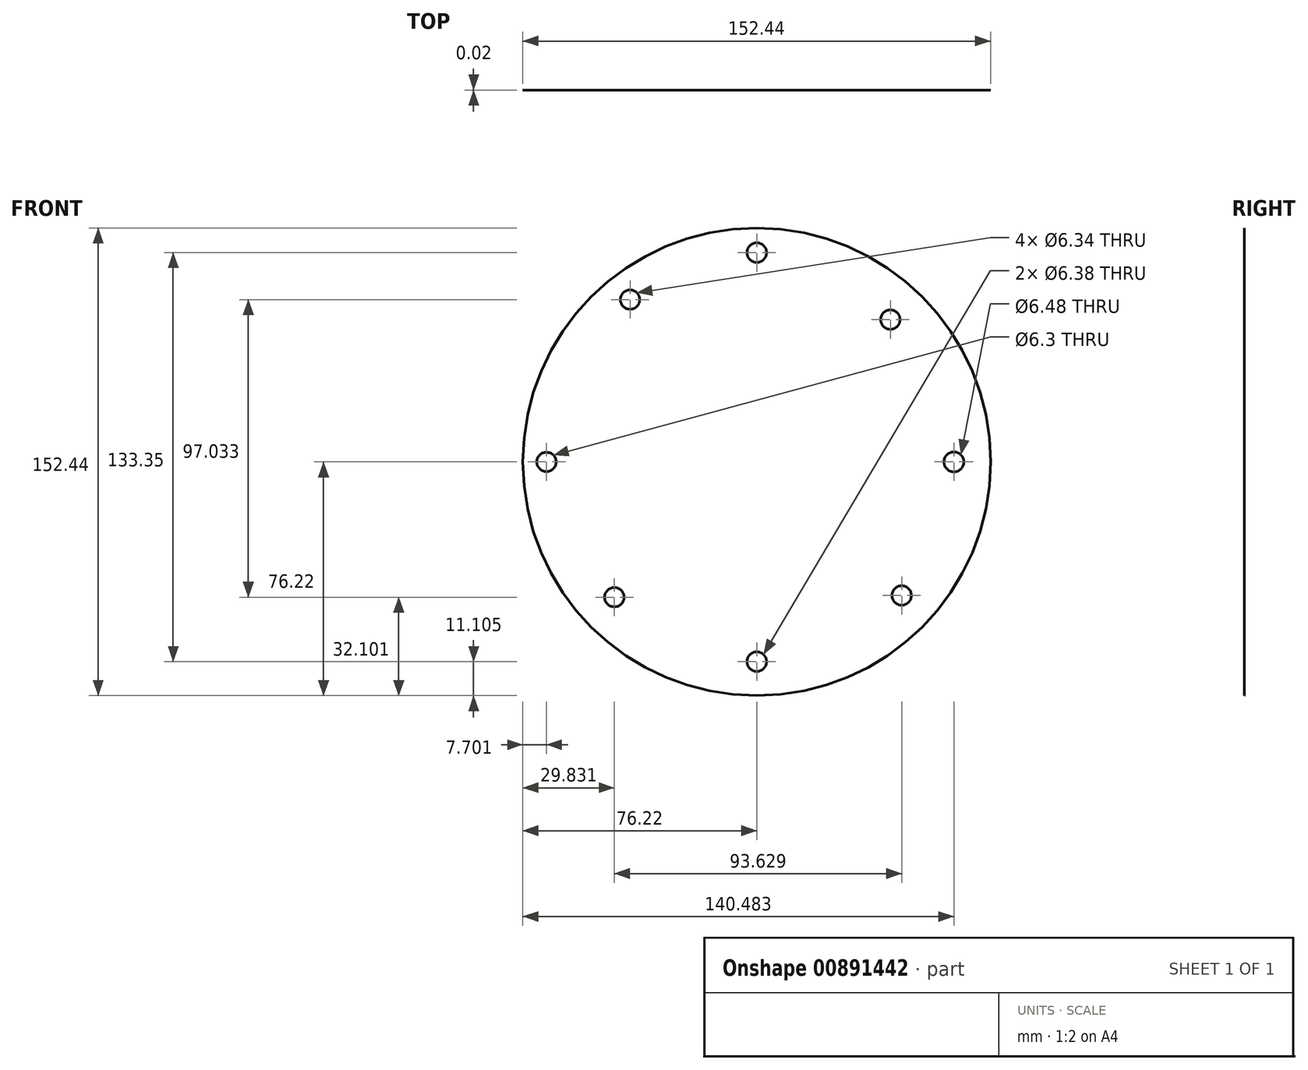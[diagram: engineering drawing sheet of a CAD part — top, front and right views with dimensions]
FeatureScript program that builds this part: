
annotation { "Feature Type Name" : "Feature", "Feature Type Description" : "" }
export const myFeature = defineFeature(function(context is Context, id is Id, definition is map)
    precondition{}
    {
        {
            var Q0;
            Q0=qCreatedBy(makeId("Front.planeOp"),FACE);
            var sketch = newSketch(context, id + "F0", { "sketchPlane" : qUnion([Q0])});
            skCircle(sketch, "E0", {"center": v(0, 0) * mm, "radius": 76.22 * mm});
            skSolve(sketch);
        }
        {
            var Q0;
            Q0=qSketchRegion(id+"F0",true);
            extrude(context, id + "F1", {"entities" : qUnion([Q0]), "depth" : 1 / 50.8 * mm, "offsetDistance" : 25.4 * mm});
        }
        {
            var Q0;
            Q0=qCreatedBy(makeId("Front.planeOp"),FACE);
            var sketch = newSketch(context, id + "F2", { "sketchPlane" : qUnion([Q0])});
            skCircle(sketch, "E1", {"center": v(0, 68.24) * mm, "radius": 3.19 * mm});
            skCircle(sketch, "E2", {"center": v(0, -65.11) * mm, "radius": 3.19 * mm});
            skCircle(sketch, "E3", {"center": v(64.26, 0) * mm, "radius": 3.24 * mm});
            skCircle(sketch, "E4", {"center": v(-68.52, 0) * mm, "radius": 3.15 * mm});
            skCircle(sketch, "E5", {"center": v(-41.28, 52.91) * mm, "radius": 3.17 * mm});
            skCircle(sketch, "E6", {"center": v(47.24, -43.55) * mm, "radius": 3.17 * mm});
            skCircle(sketch, "E7", {"center": v(-46.39, -44.12) * mm, "radius": 3.17 * mm});
            skCircle(sketch, "E8", {"center": v(43.55, 46.39) * mm, "radius": 3.17 * mm});
            skSolve(sketch);
        }
        {
            var Q0;
            Q0=qSketchRegion(id+"F2",true);
            extrude(context, id + "F3", {"entities" : qUnion([Q0]), "operationType" : NewBodyOperationType.REMOVE, "depth" : 25.4 * mm, "offsetDistance" : 25.4 * mm});
        }
    });
